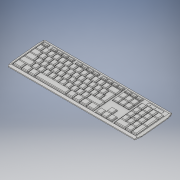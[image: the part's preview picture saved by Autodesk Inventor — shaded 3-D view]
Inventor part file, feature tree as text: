
AUTODESK INVENTOR PART (.ipt)
format: ipt  version: 2017 (Build 210142000, 142)  size: 3,179,008 bytes
history: native  units: in
note: dims shown in document units (in); Inventor stores cm internally (conversion verified against a paired STEP export)
features: other x111, loft x104, extrude x17, sketch x15, mirror x3, plane x2, fillet x1
ambient origin geometry x8: Origin, YZ Plane, XZ Plane, XY Plane, X Axis, Y Axis, Z Axis, Center Point
bodies: Solid4 (feature_tree)
feature tree (253):
  other  "key board"
  extrude  "key board to cut from"  Depth=0.4271in
  extrude  "curve top and bottom"  Depth=0.0938in
  extrude  "curve corners"  Depth=0.3125in
  other  "side curve workplane"
  extrude  "right curve edge"  Depth=0.0053in
  mirror  "mirror plane"
  mirror  "mirror right edge"
  other  "right curve workplane"
  extrude  "right curve diaganal"  Depth=0.0163in
  mirror  "mirror curve right"
  extrude  "leftover from diaganal and right curve"  Depth=0.0238in
  extrude  "back curve corner"  Depth=0.009in
  extrude  "ramp for keys"  Depth=0.0011in
  other  "ramp flushing plane"
  extrude  "ramp flushed"  Depth=0.015in
  extrude  "ramp random extion"  Depth=0.0153in
  plane  "Work Plane9"
  extrude  "top side curve"  Depth=1.0in TaperAngle=0.0deg
  extrude  "key slots"  Depth=0.0208in
  other  "keys workplane"
  extrude  "bottom of keys"  Depth=0.0036in
  plane  "Work Plane10"
  sketch  "Sketch23"  dims[d45=90.0deg d55=0.0208in]
  extrude  "Caps lock and Num Lock light indicators cut out"  Depth=1.0in TaperAngle=0.0deg
  sketch  "Sketch25"  dims[d58=0.7136in d67=1.0in d68=0.0in]
  extrude  "light indicators cut out"  Depth=0.0036in
  extrude  "light indicators join"  Depth=0.0005in TaperAngle=0.0deg
  loft  "`~ key"
  loft  "1! key"
  loft  "2@ key"
  loft  "3# key"
  loft  "4$ key"
  loft  "5% key"
  loft  "6^ key"
  loft  "7& key"
  loft  "8* key"
  loft  "9( key"
  loft  "0) key"
  loft  "-_ key"
  loft  "=+ key"
  loft  "Q key"
  loft  "W key"
  loft  "E key"
  loft  "R key"
  loft  "T key"
  loft  "Y key"
  loft  "U key"
  loft  "I key"
  loft  "O key"
  loft  "P key"
  loft  "[{ key"
  loft  "]} key"
  loft  "\| key"
  loft  "'" key"
  loft  ";: key"
  loft  "L key"
  loft  "K key"
  loft  "J key"
  loft  "H key"
  loft  "G key"
  loft  "F key"
  loft  "D key"
  loft  "S key"
  loft  "A key"
  loft  "Z key"
  loft  "X key"
  loft  "C key"
  loft  "V key"
  loft  "B key"
  loft  "N key"
  loft  "M key"
  loft  ",< key"
  loft  ".> key"
  loft  "/? key"
  loft  "Tab  key"
  loft  "Caps Lock  key"
  loft  "Left Shift key"
  loft  "Left Ctrl key"
  loft  "Left FN  key"
  loft  "Left Alt"
  loft  "space bar key"
  loft  "Right Alt  key"
  loft  "Windows  key"
  loft  "Menu  key"
  loft  "Right Ctrl  key"
  loft  "Right Shift  key"
  loft  "Enter  key"
  loft  "Backspace  key"
  loft  "Esc  key"
  loft  "F1  key"
  loft  "F2  key"
  loft  "F3  key"
  loft  "F4  key"
  loft  "F5  key"
  loft  "F6 key"
  loft  "F7 key"
  loft  "F8 key"
  loft  "F9 key"
  loft  "F10  key"
  loft  "F11  key"
  loft  "F12  key"
  loft  "Print Screen  key"
  loft  "Scroll Lock  key"
  loft  "Pause Break  key"
  loft  "Insert  key"
  loft  "Delete  key"
  loft  "End  key"
  loft  "Home  key"
  loft  "Page UP  key"
  loft  "Page Down  key"
  loft  "Up Arrow  key"
  loft  "Left Arrow  key"
  loft  "Down Arrow  key"
  loft  "Right Arrow  key"
  loft  "Num Lock  key"
  loft  "Num /  key"
  loft  "Num *  key"
  loft  "Num -  key"
  loft  "Num +  key"
  loft  "Num Enter  key"
  loft  "Num .  key"
  loft  "Num 1  key"
  loft  "Num 2  key"
  loft  "Num 3  key"
  loft  "Num 4  key"
  loft  "Num 5  key"
  extrude  "little knobs for blind"  Depth=0.1063in
  fillet  "Fillet little knobs"  Radius=0.0041in
  loft  "Num 6  key"
  loft  "Num 7  key"
  loft  "Num 8  key"
  loft  "Num 9  key"
  loft  "Num 0  key"
  other  "put in middle of terminal"
  other  "middle of the key board front to back"
  sketch  "Sketch3"  dims[d12=1.4896in d13=0.4271in]
  sketch  "Sketch4"  dims[d14=0.0749in d15=0.0in d16=0.0938in]
  sketch  "Sketch5"  dims[d17=0.032in d18=0.3125in]
  sketch  "Sketch6"  dims[d19=0.0053in d20=0.0053in]
  sketch  "Sketch8"  dims[d22=0.0036in d23=0.0163in]
  sketch  "Sketch15"  dims[d25=0.0238in d29=0.0238in]
  sketch  "Sketch16"  dims[d30=0.032in d32=0.009in]
  sketch  "Sketch18"  dims[d33=0.0092in d34=0.0011in]
  sketch  "Sketch19"  dims[d36=1.0in d37=0.0in d39=0.015in]
  sketch  "Sketch21"  dims[d40=0.0666in d41=0.0153in]
  sketch  "Sketch22"  dims[d42=0.0621in d43=1.0in d44=0.0in]
  other  "Edges1"
  other  "Edges2"
  other  "Edges3"
  other  "Edges4"
  other  "Edges5"
  other  "Edges6"
  other  "Edges7"
  other  "Edges8"
  other  "Edges9"
  other  "Edges10"
  other  "Edges11"
  other  "Edges12"
  other  "Edges13"
  other  "Edges14"
  other  "Edges15"
  other  "Edges16"
  other  "Edges17"
  other  "Edges18"
  other  "Edges19"
  other  "Edges20"
  other  "Edges21"
  other  "Edges22"
  other  "Edges23"
  other  "Edges24"
  other  "Edges25"
  other  "Edges26"
  other  "Edges27"
  other  "Edges28"
  other  "Edges29"
  other  "Edges30"
  other  "Edges31"
  other  "Edges32"
  other  "Edges33"
  other  "Edges34"
  other  "Edges35"
  other  "Edges36"
  other  "Edges37"
  other  "Edges38"
  other  "Edges39"
  other  "Edges40"
  other  "Edges41"
  other  "Edges42"
  other  "Edges43"
  other  "Edges44"
  other  "Edges45"
  other  "Edges46"
  other  "Edges47"
  other  "Edges48"
  other  "Edges49"
  other  "Edges50"
  other  "Edges51"
  other  "Edges52"
  other  "Edges53"
  other  "Edges54"
  other  "Edges55"
  other  "Edges56"
  other  "Edges57"
  other  "Edges58"
  other  "Edges59"
  other  "Edges60"
  other  "Edges61"
  other  "Edges62"
  other  "Edges63"
  other  "Edges64"
  other  "Edges65"
  other  "Edges66"
  other  "Edges67"
  other  "Edges68"
  other  "Edges69"
  other  "Edges70"
  other  "Edges71"
  other  "Edges72"
  other  "Edges73"
  other  "Edges74"
  other  "Edges75"
  other  "Edges76"
  other  "Edges77"
  other  "Edges78"
  other  "Edges79"
  other  "Edges80"
  other  "Edges81"
  other  "Edges82"
  other  "Edges83"
  other  "Edges84"
  other  "Edges85"
  other  "Edges86"
  other  "Edges87"
  other  "Edges88"
  other  "Edges89"
  other  "Edges90"
  other  "Edges91"
  other  "Edges92"
  other  "Edges93"
  other  "Edges94"
  other  "Edges95"
  other  "Edges96"
  other  "Edges97"
  other  "Edges98"
  other  "Edges99"
  other  "Edges100"
  other  "Edges101"
  other  "Edges102"
  other  "Edges103"
  other  "Edges104"
  sketch  "Sketch24"  dims[d56=0.0053in d57=0.0036in]
  sketch  "Sketch26"  dims[d73=0.0053in d74=0.0036in d76=1.0in d77=0.0in d78=1.0in d79=0.0in d81=0.0058in d82=0.0058in d90=0.0307in d91=0.0307in d94=0.017in d95=0.0653in d96=0.0653in d97=0.0653in d98=0.0653in d99=0.0653in d100=0.017in d101=0.1958in d102=0.1305in d104=0.3262in d106=0.0746in d108=0.0083in d109=0.261in d111=0.0262in d112=0.261in d113=0.0262in d114=0.261in d115=0.02in d116=0.0in d117=0.0083in d118=0.0592in d119=0.0592in d120=0.0592in d121=0.0592in d122=0.0592in d123=0.0592in d124=0.0592in d125=0.0592in d126=0.0592in d127=0.0592in d128=0.0592in d129=0.0592in d130=0.0592in d131=0.0592in d132=0.0041in d133=0.0041in d134=0.0041in d135=0.0041in d136=0.0041in d137=0.0041in d138=0.0041in d139=0.0041in d146=0.0592in d147=0.0592in d148=0.0592in d149=0.0592in d150=0.0592in d151=0.0592in d152=0.0592in d153=0.0592in d154=0.0592in d155=0.0592in d156=0.0592in d157=0.0592in d160=0.0041in d161=0.0041in d162=0.0041in d163=0.0041in d164=0.0041in d166=0.0041in d167=0.0041in d172=0.0041in d173=0.032in d174=0.017in d175=1.0in d176=0.0in d177=0.066in d178=0.066in d179=0.0686in d180=0.0686in d183=90.0deg d184=1.0in d185=0.0in d186=0.0328in d187=0.0031in d188=0.0031in d189=0.063in d190=0.0328in d191=0.0031in d192=0.0031in d193=0.063in d194=1.0in d195=0.0in d196=0.0041in d197=0.1095in d198=0.0041in d199=0.0041in d200=0.0041in d201=0.0041in d202=0.0041in d203=0.0041in d204=0.0041in d205=0.0592in d206=0.0592in d207=0.0592in d208=0.0592in d209=0.0041in d210=0.0041in d213=0.0304in d214=90.0deg d215=0.0091in d216=0.0249in d217=0.0091in d218=0.0249in d219=1.0in d220=0.0in d222=0.0041in d226=0.0592in d227=0.0592in d228=0.0592in d229=0.0592in d230=0.0041in d231=0.0041in d232=0.0041in d233=0.0041in d234=0.0592in d235=0.0041in d236=0.0041in d237=0.0041in d238=0.0592in d239=0.0592in d240=0.0592in d241=0.0592in d242=0.0041in d243=0.0041in d244=0.0041in d248=0.0592in d249=0.0041in d250=0.0041in d251=0.0041in d252=0.0041in d253=0.0041in d254=0.1958in d255=0.017in d256=0.0592in d257=0.0592in d258=0.0592in d260=0.0041in d261=0.0041in d263=0.0592in d264=0.0041in d265=0.0041in d267=0.0592in d268=0.0592in d269=0.0592in d270=0.0592in d271=0.0592in d272=0.0592in d273=0.0592in d274=0.0592in d275=0.0592in d276=0.0592in d277=0.0592in d278=0.0592in d279=0.0592in d280=0.0592in d281=0.0041in d282=0.0041in d283=0.0041in d284=0.0041in d285=0.0041in d286=0.0041in d287=0.0592in d288=0.0592in d289=0.0592in d290=0.0592in d291=0.0592in d292=0.0592in d293=0.0592in d294=0.0592in d295=0.0592in d296=0.0592in d297=0.0041in d298=0.0041in d299=0.0041in d300=0.0041in d301=0.0041in d302=0.0041in d303=0.0041in d304=0.0592in d305=0.0041in d306=0.0041in d307=0.0902in d308=0.0592in d310=0.0041in d311=0.0592in d312=0.1063in d313=0.0041in d314=0.0592in d315=0.0592in d316=0.0592in d317=0.0592in d318=0.0592in d319=0.0592in d320=0.0592in d321=0.0592in d322=0.0592in d323=0.0592in d324=0.0592in d325=0.0592in d326=0.0592in d327=0.0592in d328=0.0041in d329=0.0041in d330=0.0041in d331=0.0041in d332=0.0041in d333=0.0041in d334=0.0592in d335=0.0592in d336=0.0592in d337=0.0592in d338=0.0592in d339=0.0592in d340=0.0592in d341=0.0592in d342=0.0592in d343=0.0592in d344=0.0041in d345=0.0041in d346=0.0041in d347=0.0041in d348=0.0041in d349=0.0592in d350=0.0041in d351=0.0041in d352=0.0041in d353=0.0041in d354=0.0592in d355=0.0592in d356=0.0592in d357=0.0592in d358=0.0592in d359=0.0592in d360=0.0592in d361=0.0592in d362=0.0592in d363=0.0592in d364=0.0592in d365=0.0592in d366=0.0592in d367=0.0592in d368=0.0041in d369=0.0041in d370=0.0041in d371=0.0041in d372=0.0041in d373=0.0041in d374=0.0592in d375=0.0592in d376=0.0592in d377=0.0592in d378=0.0592in d379=0.0592in d380=0.0041in d381=0.0041in d382=0.0041in d383=0.0592in d384=0.0041in d385=0.0041in d386=0.0592in d387=0.0041in d388=0.1355in d389=0.0041in d392=0.0041in d393=0.0592in d394=0.0899in d395=0.0041in d396=0.0041in d397=0.0041in d398=0.0041in d399=0.0041in d400=0.0041in d401=0.0747in d402=0.0747in d403=0.3529in d404=0.0743in d405=0.0755in d406=0.0041in d407=0.0041in d408=0.0747in d410=0.0592in d411=0.0592in d412=0.0592in d413=0.0592in d414=0.0041in d415=0.0592in d416=0.0041in d417=0.0592in d418=0.0592in d419=0.0592in d420=0.0592in d421=0.0041in d422=0.0592in d423=0.0041in d424=0.0592in d425=0.0592in d426=0.0592in d427=0.0592in d428=0.0041in d429=0.0592in d430=0.0041in d431=0.0592in d432=0.0592in d433=0.0592in d434=0.0592in d435=0.0041in d436=0.0592in d437=0.0041in d438=0.0592in d439=0.0592in d440=0.0592in d441=0.0592in d442=0.0041in d443=0.0592in d444=0.0041in d445=0.0592in d446=0.0592in d447=0.0592in d448=0.0592in d449=0.0041in d450=0.0592in d451=0.0041in d452=0.0592in d453=0.0592in d454=0.0592in d455=0.0592in d456=0.0041in d457=0.0592in d458=0.0041in d459=0.0592in d460=0.0592in d461=0.0592in d462=0.0592in d463=0.0041in d464=0.0592in d465=0.0041in d466=0.0041in d467=0.0041in d468=0.0041in d469=0.0041in d470=0.0041in d471=0.0041in d472=0.0041in d473=0.0041in d474=0.0041in d475=0.0041in d476=0.0041in d477=0.0592in d478=0.0592in d479=0.0592in d480=0.0592in d481=0.0592in d482=0.0592in d483=0.0592in d484=0.0592in d485=0.0592in d486=0.0592in d487=0.0592in d488=0.0592in d489=0.0041in d490=0.0041in d491=0.0041in d492=0.0041in d495=0.032in d496=0.0592in d497=0.0592in d498=0.0592in d499=0.0592in d500=0.0592in d501=0.0592in d502=0.0041in d503=0.0041in d504=0.0592in d505=0.0592in d506=0.0592in d507=0.0592in d508=0.0592in d509=0.0592in d510=0.0041in d512=0.0208in d513=0.0091in d514=1.0in d515=0.0in d516=0.0592in d517=0.0592in d518=0.0592in d519=0.0592in d520=0.0592in d522=0.0592in d523=0.0592in d525=0.0592in d526=0.0592in d527=0.0592in d528=0.0592in d530=0.0592in d531=0.0592in d533=0.0592in d534=0.0592in d535=0.0592in d536=0.0592in d538=0.0592in d540=0.0134in d541=0.0in d542=0.0083in d901=0.0246in d905=0.0271in d906=0.021in d909=0.0246in d910=0.0271in d911=0.021in d912=0.0592in d1093=0.0246in d1094=0.0271in d1095=0.021in d1096=0.0592in d1097=0.0246in d1098=0.0271in d1099=0.021in d1100=0.0592in d1101=0.0246in d1102=0.0271in d1103=0.021in d1104=0.0592in d1105=0.0246in d1106=0.0271in d1107=0.021in d1108=0.0592in d1109=0.0246in d1110=0.0271in d1111=0.021in d1112=0.0592in d1113=0.0246in d1114=0.0271in d1115=0.021in d1116=0.0592in d1117=0.0246in d1118=0.0271in d1119=0.021in d1120=0.0592in d1121=0.0246in d1122=0.0271in d1123=0.021in d1124=0.0592in d1125=0.0246in d1126=0.0271in d1127=0.021in d1128=0.0592in d1129=0.0246in d1130=0.0271in d1131=0.021in d1132=0.0592in d1133=0.0246in d1134=0.0271in d1135=0.021in d1136=0.0592in d1137=0.0246in d1138=0.0271in d1139=0.021in d1140=0.0592in d1141=0.0246in d1142=0.0271in d1143=0.021in d1144=0.0592in d1145=0.0246in d1146=0.0271in d1147=0.021in d1148=0.0592in d1149=0.0246in d1150=0.0271in d1151=0.021in d1152=0.0592in d1153=0.0246in d1154=0.0271in d1155=0.021in d1156=0.0592in d1157=0.0246in d1158=0.0271in d1159=0.021in d1160=0.0592in d1161=0.0246in d1162=0.0271in d1163=0.021in d1164=0.0592in d1165=0.0246in d1166=0.0271in d1167=0.021in d1168=0.0592in d1169=0.0246in d1170=0.0271in d1171=0.021in d1172=0.0592in d1173=0.0246in d1174=0.0271in d1175=0.021in d1176=0.0592in d1177=0.0246in d1178=0.0271in d1179=0.021in d1180=0.0592in d1181=0.0246in d1182=0.0271in d1183=0.021in d1184=0.0592in d1185=0.0246in d1186=0.0271in d1187=0.021in d1188=0.0592in d1189=0.0246in d1190=0.0271in d1191=0.021in d1192=0.0592in d1193=0.0246in d1194=0.0271in d1195=0.021in d1196=0.0592in d1197=0.0246in d1198=0.0271in d1199=0.021in d1200=0.0592in d1201=0.0246in d1202=0.0271in d1203=0.021in d1204=0.0592in d1205=0.0246in d1206=0.0271in d1207=0.021in d1208=0.0592in d1209=0.0246in d1210=0.0271in d1211=0.021in d1212=0.0592in d1213=0.0246in d1214=0.0271in d1215=0.021in d1216=0.0592in d1217=0.0246in d1218=0.0271in d1219=0.021in d1220=0.0592in d1221=0.0246in d1222=0.0271in d1223=0.021in d1224=0.0592in d1225=0.0246in d1226=0.0271in d1227=0.021in d1228=0.0592in d1229=0.0246in d1230=0.0271in d1231=0.021in d1232=0.0592in d1233=0.0246in d1234=0.0271in d1235=0.021in d1236=0.0592in d1237=0.0246in d1238=0.0271in d1239=0.021in d1240=0.0592in d1241=0.0246in d1242=0.0271in d1243=0.021in d1244=0.0592in d1245=0.0246in d1246=0.0271in d1247=0.021in d1248=0.0592in d1249=0.0246in d1250=0.0271in d1251=0.021in d1252=0.0592in d1253=0.0246in d1254=0.0271in d1255=0.021in d1256=0.0592in d1257=0.0246in d1258=0.0271in d1259=0.021in d1260=0.0592in d1261=0.0246in d1262=0.0271in d1263=0.021in d1264=0.0592in d1265=0.0246in d1266=0.0271in d1267=0.021in d1268=0.0592in d1269=0.0246in d1270=0.0271in d1271=0.021in d1272=0.0592in d1273=0.0in d1274=90.0deg d1275=0.0in d1276=90.0deg d1277=0.0in d1278=90.0deg d1279=0.0in d1280=90.0deg d1281=0.0in d1282=90.0deg d1283=0.0in d1284=90.0deg d1285=0.0in d1286=90.0deg d1287=0.0in d1288=90.0deg d1289=0.0in d1290=90.0deg d1291=0.0in d1292=90.0deg d1293=0.0in d1294=90.0deg d1295=0.0in d1296=90.0deg d1297=0.0in d1298=90.0deg d1299=0.0in d1300=90.0deg d1301=0.0in d1302=90.0deg d1303=0.0in d1304=90.0deg d1305=0.0in d1306=90.0deg d1307=0.0in d1308=90.0deg d1309=0.0in d1310=90.0deg d1311=0.0in d1312=90.0deg d1313=0.0in d1314=90.0deg d1315=0.0in d1316=90.0deg d1317=0.0in d1318=90.0deg d1319=0.0in d1320=90.0deg d1321=0.0in d1322=90.0deg d1323=0.0in d1324=90.0deg d1325=0.0in d1326=90.0deg d1327=0.0in d1328=90.0deg d1329=0.0in d1330=90.0deg d1331=0.0in d1332=90.0deg d1333=0.0in d1334=90.0deg d1335=0.0in d1336=90.0deg d1337=0.0in d1338=90.0deg d1339=0.0in d1340=90.0deg d1341=0.0in d1342=90.0deg d1343=0.0in d1344=90.0deg d1345=0.0in d1346=90.0deg d1347=0.0in d1348=90.0deg d1349=0.0in d1350=90.0deg d1351=0.0in d1352=90.0deg d1353=0.0in d1354=90.0deg d1355=0.0in d1356=90.0deg d1357=0.0in d1358=90.0deg d1359=0.0in d1360=90.0deg d1361=0.0in d1362=90.0deg d1363=0.0in d1364=90.0deg d1365=0.0in d1366=90.0deg d1367=0.0in d1368=90.0deg d1369=0.0in d1370=90.0deg d1371=0.0in d1372=90.0deg d1373=0.0in d1374=90.0deg d1375=0.0in d1376=90.0deg d1377=0.0in d1378=90.0deg d1379=0.0in d1380=90.0deg d1381=0.0in d1382=90.0deg d1383=0.0in d1384=90.0deg d1385=0.0in d1386=90.0deg d1387=0.0in d1388=90.0deg d1389=0.0in d1390=90.0deg d1391=0.0in d1392=90.0deg d1393=0.0in d1394=90.0deg d1395=0.0in d1396=90.0deg d1397=0.0in d1398=90.0deg d1399=0.0in d1400=90.0deg d1401=0.0in d1402=90.0deg d1403=0.0in d1404=90.0deg d1405=0.0in d1406=90.0deg d1407=0.0in d1408=90.0deg d1409=0.0in d1410=90.0deg d1411=0.0in d1412=90.0deg d1413=0.0in d1414=90.0deg d1415=0.0in d1416=90.0deg d1417=0.0in d1418=90.0deg d1419=0.0in d1420=90.0deg d1421=0.0in d1422=90.0deg d1423=0.0in d1424=90.0deg d1425=0.0in d1426=90.0deg d1427=0.0in d1428=90.0deg d1429=0.0in d1430=90.0deg d1431=0.0in d1432=90.0deg d1433=0.0in d1434=90.0deg d1435=0.0in d1436=90.0deg d1437=0.0in d1438=90.0deg d1439=0.0in d1440=90.0deg d1441=0.0in d1442=90.0deg d1443=0.0in d1444=90.0deg d1445=0.0in d1446=90.0deg d1447=0.0in d1448=90.0deg d1449=0.0in d1450=90.0deg d1451=0.0in d1452=90.0deg d1453=0.0in d1454=90.0deg d1455=0.0in d1456=90.0deg d1457=0.0in d1458=90.0deg d1459=0.0in d1460=90.0deg d1463=0.0246in d1464=0.0271in d1465=0.0365in d1466=0.0592in d1467=0.0246in d1468=0.0271in d1469=0.0445in d1470=0.0592in d1471=0.0902in d1473=0.0246in d1474=0.0271in d1475=0.0591in d1476=0.0592in d1477=0.1063in d1479=0.0246in d1480=0.0271in d1481=0.0461in d1482=0.0592in d1484=0.0246in d1485=0.0271in d1486=0.0363in d1487=0.0592in d1488=0.1355in d1489=0.0246in d1490=0.0271in d1491=0.0287in d1492=0.0592in d1493=0.0899in d1494=0.0246in d1495=0.0271in d1496=0.0288in d1497=0.0592in d1498=0.0899in d1499=0.0246in d1500=0.0271in d1501=0.1678in d1502=0.0592in d1503=0.0899in d1504=0.0246in d1505=0.0271in d1506=0.0285in d1507=0.0592in d1508=0.0899in d1509=0.0246in d1510=0.0271in d1511=0.0291in d1512=0.0592in d1513=0.0899in d1514=0.0246in d1515=0.0271in d1516=0.0288in d1517=0.0592in d1518=0.0899in d1519=0.0246in d1520=0.0271in d1521=0.0348in d1522=0.0592in d1523=0.0899in d1524=0.0246in d1525=0.0271in d1526=0.0713in d1527=0.0592in d1528=0.0899in d1529=0.0869in d1530=0.1598in d1532=0.0271in d1533=0.0306in d1534=0.0592in d1535=0.0246in d1538=0.0592in d1539=0.0785in d1540=0.0624in d1541=0.0226in d1542=0.0in d1543=90.0deg d1544=0.0in d1545=90.0deg d1546=0.0in d1547=90.0deg d1548=0.0in d1549=90.0deg d1550=0.0in d1551=90.0deg d1552=0.0in d1553=90.0deg d1554=0.0in d1555=90.0deg d1556=0.0in d1557=90.0deg d1558=0.0in d1559=90.0deg d1560=0.0in d1561=90.0deg d1562=0.0in d1563=90.0deg d1564=0.0in d1565=90.0deg d1566=0.0in d1567=90.0deg d1568=0.0in d1569=90.0deg d1570=0.0in d1571=90.0deg d1572=0.0in d1573=90.0deg d1574=0.0in d1575=90.0deg d1576=0.0in d1577=90.0deg d1578=0.0in d1579=90.0deg d1580=0.0in d1581=90.0deg d1582=0.0in d1583=90.0deg d1584=0.0in d1585=90.0deg d1586=0.0in d1587=90.0deg d1588=0.0in d1589=90.0deg d1590=0.0in d1591=90.0deg d1592=0.0in d1593=90.0deg d1594=0.0in d1595=90.0deg d1596=0.0in d1597=90.0deg d1598=0.0664in d1599=0.0251in d1602=0.0101in d1603=0.0076in d1604=0.0246in d1605=0.0101in d1606=0.0076in d1607=0.0246in d1608=0.0251in d1609=0.0664in d1610=0.0101in d1611=0.0076in d1612=0.0246in d1613=0.0251in d1614=0.0664in d1615=0.0101in d1616=0.0076in d1617=0.0246in d1618=0.0251in d1619=0.0664in d1620=0.0101in d1621=0.0076in d1622=0.0246in d1623=0.0251in d1624=0.0664in d1625=0.0101in d1626=0.0076in d1627=0.0246in d1628=0.0251in d1629=0.0664in d1630=0.0101in d1631=0.0076in d1632=0.0246in d1633=0.0251in d1634=0.0664in d1635=0.0101in d1636=0.0076in d1637=0.0246in d1638=0.0251in d1639=0.0664in d1640=0.0101in d1641=0.0076in d1642=0.0246in d1643=0.0251in d1644=0.0664in d1645=0.0101in d1646=0.0076in d1647=0.0246in d1648=0.0251in d1649=0.0664in d1650=0.0101in d1651=0.0076in d1652=0.0246in d1653=0.0251in d1654=0.0664in d1655=0.0101in d1656=0.0076in d1657=0.0246in d1658=0.0251in d1659=0.0664in d1660=0.0101in d1661=0.0076in d1662=0.0246in d1663=0.0251in d1664=0.0664in d1665=0.0101in d1666=0.0076in d1667=0.0246in d1668=0.0251in d1669=0.0664in d1670=0.0101in d1671=0.0076in d1672=0.0246in d1673=0.0251in d1674=0.0664in d1675=0.0101in d1676=0.0076in d1677=0.0246in d1678=0.0251in d1679=0.0664in d1680=0.0in d1681=90.0deg d1682=0.0in d1683=90.0deg d1684=0.0in d1685=90.0deg d1686=0.0in d1687=90.0deg d1688=0.0in d1689=90.0deg d1690=0.0in d1691=90.0deg d1692=0.0in d1693=90.0deg d1694=0.0in d1695=90.0deg d1696=0.0in d1697=90.0deg d1698=0.0in d1699=90.0deg d1700=0.0in d1701=90.0deg d1702=0.0in d1703=90.0deg d1704=0.0in d1705=90.0deg d1706=0.0in d1707=90.0deg d1708=0.0in d1709=90.0deg d1710=0.0in d1711=90.0deg d1712=0.0in d1713=90.0deg d1714=0.0in d1715=90.0deg d1716=0.0in d1717=90.0deg d1718=0.0in d1719=90.0deg d1720=0.0in d1721=90.0deg d1722=0.0in d1723=90.0deg d1724=0.0in d1725=90.0deg d1726=0.0in d1727=90.0deg d1728=0.0in d1729=90.0deg d1730=0.0in d1731=90.0deg d1732=0.0in d1733=90.0deg d1734=0.0in d1735=90.0deg d1736=0.0in d1737=90.0deg d1738=0.0in d1739=90.0deg d1740=0.0in d1741=90.0deg d1742=0.0in d1743=90.0deg d1744=0.0271in d1745=0.0246in d1746=0.0246in d1747=0.0251in d1748=0.0664in d1749=0.0271in d1750=0.0246in d1751=0.0246in d1752=0.0251in d1753=0.0664in d1754=0.0271in d1755=0.0246in d1756=0.0246in d1757=0.0251in d1758=0.0664in d1759=0.0271in d1760=0.0246in d1761=0.0246in d1762=0.0251in d1763=0.0664in d1764=0.0271in d1765=0.0246in d1766=0.0246in d1767=0.0251in d1768=0.0664in d1769=0.0271in d1770=0.0246in d1771=0.0246in d1772=0.0251in d1773=0.0664in d1774=0.0271in d1775=0.0246in d1776=0.0246in d1777=0.0592in d1778=0.0664in d1779=0.0592in d1780=0.0271in d1781=0.0246in d1782=0.0246in d1783=0.0592in d1784=0.0664in d1785=0.0592in d1792=0.0271in d1793=0.0246in d1794=0.0246in d1795=0.0592in d1796=0.0664in d1797=0.0592in d1798=0.0271in d1799=0.0246in d1800=0.021in d1801=0.0592in d1802=0.0664in d1803=0.0592in d1804=0.0271in d1805=0.0246in d1806=0.021in d1807=0.0592in d1808=0.0664in d1809=0.0592in d1810=0.0271in d1811=0.0246in d1812=0.021in d1813=0.0592in d1814=0.0664in d1815=0.0592in d1816=0.0271in d1817=0.0246in d1818=0.021in d1819=0.0592in d1820=0.0664in d1821=0.0592in d1822=0.0271in d1823=0.0246in d1824=0.021in d1825=0.0592in d1826=0.0664in d1827=0.0592in d1828=0.0271in d1829=0.0246in d1830=0.021in d1831=0.0592in d1832=0.0664in d1833=0.0592in d1834=0.0271in d1835=0.0246in d1836=0.021in d1837=0.0592in d1838=0.0664in d1839=0.0592in d1840=0.0271in d1841=0.0246in d1842=0.021in d1843=0.0592in d1844=0.0664in d1845=0.0592in d1846=0.0271in d1847=0.0246in d1848=0.021in d1849=0.0592in d1850=0.0664in d1851=0.0592in d1852=0.0271in d1853=0.0246in d1854=0.021in d1855=0.0592in d1856=0.0664in d1857=0.0592in d1858=0.0271in d1859=0.0246in d1860=0.021in d1861=0.0592in d1862=0.0664in d1863=0.0592in d1864=0.0271in d1865=0.0246in d1866=0.021in d1867=0.0592in d1868=0.0664in d1869=0.0592in d1870=0.0271in d1871=0.0246in d1872=0.021in d1873=0.0592in d1874=0.0664in d1875=0.0592in d1876=0.0271in d1877=0.0246in d1878=0.0246in d1879=0.0592in d1880=0.0664in d1881=0.0592in d1882=0.0271in d1883=0.0246in d1884=0.0246in d1885=0.0592in d1886=0.0664in d1887=0.0592in d1888=0.0271in d1889=0.0246in d1890=0.0526in d1891=0.0592in d1892=0.0664in d1893=0.0592in d1900=0.0588in d1901=0.0563in d1902=0.021in d1903=0.0592in d1904=0.0664in d1905=0.0592in d1912=0.1225in d1913=0.1225in d1914=0.1225in d1915=0.0588in d1916=0.0563in d1917=0.021in d1918=0.0592in d1919=0.0592in d1920=0.0592in d1921=0.0592in d1922=0.0in d1923=90.0deg d1924=0.0in d1925=90.0deg d1926=0.0in d1927=90.0deg d1928=0.0in d1929=90.0deg d1930=0.0in d1931=90.0deg d1932=0.0in d1933=90.0deg d1934=0.0in d1935=90.0deg d1936=0.0in d1937=90.0deg d1938=0.0in d1939=90.0deg d1940=0.0in d1941=90.0deg d1942=0.0in d1943=90.0deg d1944=0.0in d1945=90.0deg d1946=0.0in d1947=90.0deg d1948=0.0in d1949=90.0deg d1950=0.0in d1951=90.0deg d1952=0.0in d1953=90.0deg d1954=0.0in d1955=90.0deg d1956=0.0in d1957=90.0deg d1958=0.0in d1959=90.0deg d1960=0.0in d1961=90.0deg d1962=0.0in d1963=90.0deg d1964=0.0in d1965=90.0deg d1966=0.0in d1967=90.0deg d1968=0.0in d1969=90.0deg d1970=0.0in d1971=90.0deg d1972=0.0in d1973=90.0deg d1974=0.0in d1975=90.0deg d1976=0.0in d1977=90.0deg d1978=0.0in d1979=90.0deg d1980=0.0in d1981=90.0deg d1982=0.0in d1983=90.0deg d1984=0.0in d1985=90.0deg d1986=0.0in d1987=90.0deg d1988=0.0in d1989=90.0deg d1990=0.0in d1991=90.0deg d1992=0.0in d1993=90.0deg d1994=0.0in d1995=90.0deg d1996=0.0in d1997=90.0deg d1998=0.0in d1999=90.0deg d2000=0.0in d2001=90.0deg d2002=0.0in d2003=90.0deg d2004=0.0in d2005=90.0deg d2006=0.0in d2007=90.0deg d2008=0.0in d2009=90.0deg d2010=0.0in d2011=90.0deg d2012=0.0in d2013=90.0deg d2014=0.0in d2015=90.0deg d2016=0.0in d2017=90.0deg d2018=0.0in d2019=90.0deg d2020=0.0in d2021=90.0deg d2022=0.0in d2023=90.0deg d2024=0.0in d2025=90.0deg d2026=0.0in d2027=90.0deg d2028=0.0in d2029=90.0deg d2033=0.0325in d2035=0.0023in d2036=0.0023in d2037=0.088in d2038=0.0581in d2039=0.0287in d2040=0.0073in d2041=0.0592in d2042=0.0013in d2043=0.0in d2044=0.0592in d2045=0.0073in d2046=0.0287in d2047=0.0013in d2048=0.0in d2049=0.0013in d2050=0.0in d2057=0.0067in d2061=0.0015in d2062=0.0112in d2063=0.0015in d2064=0.0112in d2065=0.0015in d2066=0.0112in d2067=0.0067in d2068=0.0067in d2069=0.0018in d2070=0.0in d2071=0.0005in]
